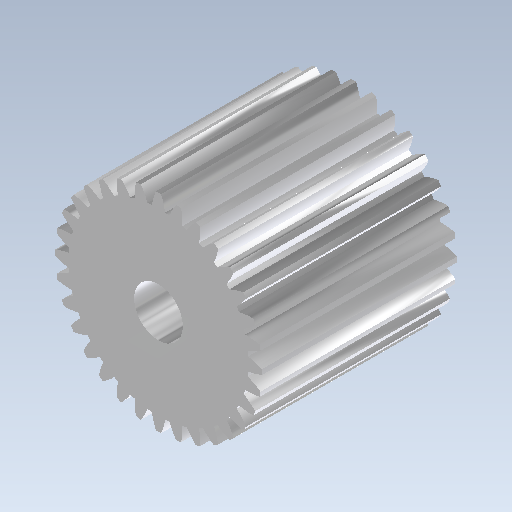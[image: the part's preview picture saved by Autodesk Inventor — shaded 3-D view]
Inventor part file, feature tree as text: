
AUTODESK INVENTOR PART (.ipt)
format: ipt  version: 2021 (Build 250183000, 183)  size: 338,432 bytes
history: native  units: mm (DEFAULTED — no unit token found)
features: plane x3, other x3, sketch x3, extrude x2
ambient origin geometry x8: Origin, YZ Plane, XZ Plane, XY Plane, X Axis, Y Axis, Z Axis, Center Point
bodies: Solid1 (feature_tree)
feature tree (11):
  extrude  "Extrusion1"  Depth=40.0mm TaperAngle=0.0deg
  plane  "Work Plane2"
  plane  "Work Plane8"
  plane  "Work Plane9"
  other  "Spur Gear"
  extrude  "Extrusion2"  Depth=10.0mm TaperAngle=0.0deg
  sketch  "Sketch1"  dims[d0=42.5mm d1=40.0mm d2=0.0mm]
  sketch  "Sketch2"  dims[d3=40.0mm d4=10.0mm d5=0.0mm]
  other  "Srf1"
  sketch  "Sketch3"  dims[d16=80.0mm d17=0.0mm d34=0.981748mm d39=0.0mm d41=0.0mm d43=80.0mm d46=80.0mm d47=0.0mm d48=0.0mm d49=10.0mm d50=40.0mm d51=0.0mm]
  other  "Pitch Diameter"
